# Revit family: Plumbing-Valves-Sloan-CROWN-120
name_source: partatom
category: Plumbing Fixtures
units: mm (PartAtom-declared; Revit-internal decimal feet)

## family parameters
Cut with Voids When Loaded = No
Host = Face
OmniClass Number = 23.45.05.14.99
OmniClass Title = Other Sanitary Washing Plumbing Fixtures
Part Type = Normal
Room Calculation Point = No
Round Connector Dimension = Use Diameter
Shared = No

## types (1)
- CROWN 120-1.6
    Assembly Code = D2020300
    CW Connection = Yes
    CWFU = 0
    Centerline of Supply from Top of Fixture = 11 1/2"
    Centerline of Supply to Centerline of Valve = 4 3/4"
    Default Elevation = 0"
    Description = 1.6 gpf, Polished Chrome Finish, Fixture Connection Rear Spud, Single
Flush, Crown® Exposed Manual Water Closet Flushometer.
    Edition number = 1
    Flush Rate = 1.6 gpf (6.0 Lpf)
    HW Connection = No
    HWFU = 0
    Height = 11 1/2"
    Keynote = 15410
    Manufacturer = Sloan Valve
    Model = CROWN 120-1.6
    Operating Water Pressure = 15 – 80 PSI (103 – 552 kPa)
    Part Number = 3120800
    Product Material = Sloan Valve - Finish - Polished Chrome
    Product data url = https://bimobject.com
    URL = www.sloanvalve.com
    Valve Pressure Drop = 0.00 psi
    Vent Connection = No
    WFU = 0
    Waste Connection = No
    Water Inlet Connection Diameter = 1"

## geometry (parser evidence)
native form markers: Sweep x6
no freeform markers — native parametric forms only
